# Revit family: Tria Light
name_source: partatom
category: Lighting Fixtures
units: mm (PartAtom-declared; Revit-internal decimal feet)

## family parameters
Always vertical = Yes
Cut with Voids When Loaded = No
Light Source = Yes
Maintain Annotation Orientation = No
OmniClass Number = 23.80.70.00
OmniClass Title = Lighting
Part Type = Normal
Room Calculation Point = No
Round Connector Dimension = Use Diameter
Shared = No
Work Plane-Based = No

## types (4) — shared parameters
CRI = 90
Color Filter = 16777215
Default Elevation = 0' - 0"
Dimming Lamp Color Temperature Shift = <None>
Input Voltage = 120-277V
Lamp = LED
Load Classification = Lighting
Manufacturer = Above All Lighting
Photometric Web File = TRIA-25-40901.ies
Power Factor = 0.9
Tilt Angle = 90.00°
URL = https://www.abovealllighting.com

## per-type parameters (varying)
| type | 180W | 25W | 40W | 90W | Model | Wattage Comments |
| TRIA-25W-4000K-WH | No | Yes | No | No | TRIA-2540901-ACPMK-WH | 25W |
| TRIA-40W-4000K-WH | No | No | Yes | No | TRIA-4040901-ACPMK-WH | 40W |
| TRIA-90W-4000K-WH | No | No | No | Yes | TRIA-9040901-ACPMK-WH | 90W |
| TRIA-180W-4000K-WH | Yes | No | No | No | TRIA-18040901-ACPMK-WH | 180W |

## geometry (parser evidence)
native form markers: Sweep x12
no freeform markers — native parametric forms only
